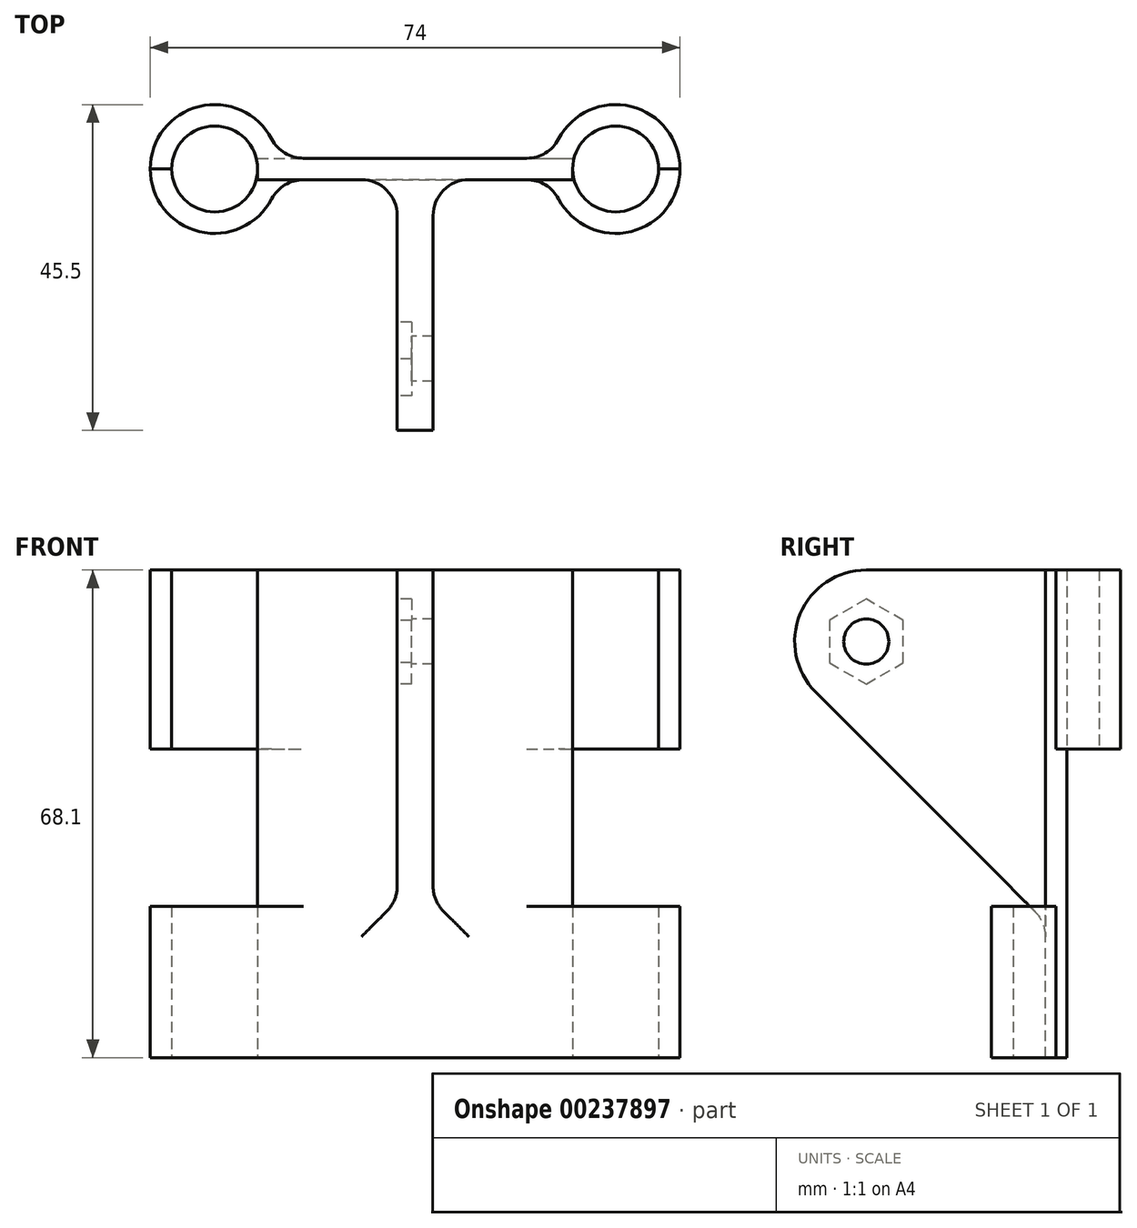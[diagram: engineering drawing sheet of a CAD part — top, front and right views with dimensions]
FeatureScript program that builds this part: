
annotation { "Feature Type Name" : "Feature", "Feature Type Description" : "" }
export const myFeature = defineFeature(function(context is Context, id is Id, definition is map)
    precondition{}
    {
        {
            var Q0;
            Q0=qCreatedBy(makeId("Top.planeOp"),FACE);
            var sketch = newSketch(context, id + "F0", { "sketchPlane" : qUnion([Q0])});
            skArc(sketch, "E0", {"start": v(-34, 0) * mm, "mid": v(-28, -6) * mm, "end": v(-22, 0) * mm});
            skArc(sketch, "E1", {"start": v(22, 0) * mm, "mid": v(28, -6) * mm, "end": v(34, 0) * mm});
            skArc(sketch, "E2", {"start": v(-37, 0) * mm, "mid": v(-28.75, -8.97) * mm, "end": v(-19.13, -1.5) * mm});
            skArc(sketch, "E3", {"start": v(19.13, -1.5) * mm, "mid": v(28.75, -8.97) * mm, "end": v(37, 0) * mm});
            skLineSegment(sketch, "E4", {"start": v(-19.13, -1.5) * mm, "end": v(19.13, -1.5) * mm});
            skLineSegment(sketch, "E5", {"start": v(-37, 0) * mm, "end": v(-34, 0) * mm});
            skLineSegment(sketch, "E6.trimOffspring", {"start": v(34, 0) * mm, "end": v(37, 0) * mm});
            skLineSegment(sketch, "E7", {"start": v(-22, 0) * mm, "end": v(-22, 1.5) * mm});
            skLineSegment(sketch, "E8", {"start": v(-22, 1.5) * mm, "end": v(22, 1.5) * mm});
            skLineSegment(sketch, "E9", {"start": v(22, 1.5) * mm, "end": v(22, 0) * mm});
            skSolve(sketch);
        }
        {
            var Q0;
            Q0=makeQuery(id+"F0.imprint","IMPRINT",FACE,{"disambiguationData":[TD([[makeQuery(id+"F0.imprint","IMPRINT",EDGE,{"derivedFrom":sQuery(id+"F0.wireOp",EDGE,"E0")}),-1.0]])]});
            extrude(context, id + "F1", {"entities" : qUnion([Q0]), "depth" : 21.1 * mm});
        }
        {
            var Q0;
            Q0=makeQuery(id+"F1.opExtrude","CAP_FACE",FACE,{"disambiguationData":[OSD([sQuery(id+"F0.wireOp",EDGE,"E0"),sQuery(id+"F0.wireOp",EDGE,"E1"),sQuery(id+"F0.wireOp",EDGE,"E2"),sQuery(id+"F0.wireOp",EDGE,"E3"),sQuery(id+"F0.wireOp",EDGE,"E4"),sQuery(id+"F0.wireOp",EDGE,"E5"),sQuery(id+"F0.wireOp",EDGE,"95d477b3-e665-48d0-b8e1-d1bc8d960a08.trimOffspring"),sQuery(id+"F0.wireOp",EDGE,"E6.trimOffspring")])],"isStart":false});
            var sketch = newSketch(context, id + "F2", { "sketchPlane" : qUnion([Q0])});
            skLineSegment(sketch, "E10.bottom", {"start": v(-22, -1.5) * mm, "end": v(22, -1.5) * mm});
            skLineSegment(sketch, "E10.top", {"start": v(-22, 1.5) * mm, "end": v(22, 1.5) * mm});
            skLineSegment(sketch, "E10.left", {"start": v(-22, -1.5) * mm, "end": v(-22, 1.5) * mm});
            skLineSegment(sketch, "E10.right", {"start": v(22, -1.5) * mm, "end": v(22, 1.5) * mm});
            skSolve(sketch);
        }
        {
            var Q0;
            Q0=makeQuery(id+"F2.imprint","IMPRINT",FACE,{"disambiguationData":[TD([[makeQuery(id+"F2.imprint","IMPRINT",EDGE,{"derivedFrom":sQuery(id+"F2.wireOp",EDGE,"E10.bottom")}),1.0]])]});
            extrude(context, id + "F3", {"entities" : qUnion([Q0]), "operationType" : NewBodyOperationType.ADD, "depth" : 22 * mm});
        }
        {
            var Q0;
            Q0=makeQuery(id+"F3.opExtrude","CAP_FACE",FACE,{"disambiguationData":[OSD([sQuery(id+"F2.wireOp",EDGE,"E10.bottom"),sQuery(id+"F2.wireOp",EDGE,"E10.top"),sQuery(id+"F2.wireOp",EDGE,"E10.left"),sQuery(id+"F2.wireOp",EDGE,"E10.right")])],"isStart":false});
            var sketch = newSketch(context, id + "F4", { "sketchPlane" : qUnion([Q0])});
            skArc(sketch, "E11", {"start": v(-22, 0) * mm, "mid": v(-28, 6) * mm, "end": v(-34, 0) * mm});
            skArc(sketch, "E12", {"start": v(34, 0) * mm, "mid": v(28, 6) * mm, "end": v(22, 0) * mm});
            skArc(sketch, "E13", {"start": v(-19.13, 1.5) * mm, "mid": v(-28.75, 8.97) * mm, "end": v(-37, 0) * mm});
            skArc(sketch, "E14", {"start": v(37, 0) * mm, "mid": v(28.75, 8.97) * mm, "end": v(19.13, 1.5) * mm});
            skLineSegment(sketch, "E15", {"start": v(-37, 0) * mm, "end": v(-34, 0) * mm});
            skPoint(sketch, "E15.startSnap0", {"position": v(-22, 0) * mm});
            skLineSegment(sketch, "E16", {"start": v(-22, 0) * mm, "end": v(-22, -1.5) * mm});
            skLineSegment(sketch, "E17", {"start": v(-22, -1.5) * mm, "end": v(22, -1.5) * mm});
            skLineSegment(sketch, "E18", {"start": v(22, 0) * mm, "end": v(22, -1.5) * mm});
            skLineSegment(sketch, "E19", {"start": v(34, 0) * mm, "end": v(37, 0) * mm});
            skLineSegment(sketch, "E20", {"start": v(-19.13, 1.5) * mm, "end": v(19.13, 1.5) * mm});
            skSolve(sketch);
        }
        {
            var Q0;
            Q0 = qSketchRegion(id + "F4", true);
            extrude(context, id + "F5", {"entities" : qUnion([Q0]), "operationType" : NewBodyOperationType.ADD, "depth" : 25 * mm});
        }
        {
            var Q0;
            Q0=qCreatedBy(makeId("Right.planeOp"),FACE);
            var sketch = newSketch(context, id + "F6", { "sketchPlane" : qUnion([Q0])});
            skArc(sketch, "E21", {"start": v(-26.5, 68.1) * mm, "mid": v(-35.74, 61.93) * mm, "end": v(-33.57, 51.03) * mm});
            skCircle(sketch, "E22", {"center": v(-26.5, 58.1) * mm, "radius": 3.15 * mm});
            skLineSegment(sketch, "E23", {"start": v(-26.5, 68.1) * mm, "end": v(0, 68.1) * mm});
            skLineSegment(sketch, "E24", {"start": v(0, 68.1) * mm, "end": v(0, 17.46) * mm});
            skLineSegment(sketch, "E25", {"start": v(0, 17.46) * mm, "end": v(-33.57, 51.03) * mm});
            skSolve(sketch);
        }
        {
            var Q0;
            Q0=makeQuery(id+"F6.imprint","IMPRINT",FACE,{"disambiguationData":[TD([[makeQuery(id+"F6.imprint","IMPRINT",EDGE,{"derivedFrom":sQuery(id+"F6.wireOp",EDGE,"E21")}),1.0]])]});
            extrude(context, id + "F7", {"entities" : qUnion([Q0]), "operationType" : NewBodyOperationType.ADD, "depth" : 5 * mm, "symmetric" : true});
        }
        {
            var Q0;
            Q0=makeQuery(id+"F7.opExtrude","CAP_FACE",FACE,{"disambiguationData":[OSD([sQuery(id+"F6.wireOp",EDGE,"E21"),sQuery(id+"F6.wireOp",EDGE,"E22"),sQuery(id+"F6.wireOp",EDGE,"E23"),sQuery(id+"F6.wireOp",EDGE,"E24"),sQuery(id+"F6.wireOp",EDGE,"E25")])],"isStart":true});
            var sketch = newSketch(context, id + "F8", { "sketchPlane" : qUnion([Q0])});
            skCircle(sketch, "E26.cCircle", {"center": v(26.5, 58.1) * mm, "radius": 5.15 * mm, "construction": true});
            skLineSegment(sketch, "E26.0", {"start": v(26.5, 64.05) * mm, "end": v(31.65, 61.07) * mm});
            skLineSegment(sketch, "E26.1", {"start": v(31.65, 61.07) * mm, "end": v(31.65, 55.13) * mm});
            skLineSegment(sketch, "E26.2", {"start": v(31.65, 55.13) * mm, "end": v(26.5, 52.15) * mm});
            skLineSegment(sketch, "E26.3", {"start": v(26.5, 52.15) * mm, "end": v(21.35, 55.13) * mm});
            skLineSegment(sketch, "E26.4", {"start": v(21.35, 55.13) * mm, "end": v(21.35, 61.07) * mm});
            skLineSegment(sketch, "E26.5", {"start": v(21.35, 61.07) * mm, "end": v(26.5, 64.05) * mm});
            skPoint(sketch, "E26.0.midPoint", {"position": v(29.08, 62.56) * mm});
            skSolve(sketch);
        }
        {
            var Q0;
            Q0=makeQuery(id+"F8.imprint","IMPRINT",FACE,{"disambiguationData":[TD([[makeQuery(id+"F8.imprint","IMPRINT",EDGE,{"derivedFrom":sQuery(id+"F8.wireOp",EDGE,"E26.0")}),-1.0]])]});
            extrude(context, id + "F9", {"entities" : qUnion([Q0]), "operationType" : NewBodyOperationType.REMOVE, "oppositeDirection" : true, "depth" : 2 * mm});
        }
        {
            var Q0;
            Q0=makeQuery(id+"F7.boolean.opBoolean","INTERSECT",EDGE,{"derivedFrom":[makeQuery(id+"F5.boolean.opBoolean","MERGE",FACE,{"derivedFrom":[makeQuery(id+"F3.boolean.opBoolean","MERGE",FACE,{"derivedFrom":[makeQuery(id+"F1.opExtrude","SWEPT_FACE",FACE,{"disambiguationData":[OSD([sQuery(id+"F0.wireOp",EDGE,"E4")])]}),makeQuery(id+"F3.opExtrude","SWEPT_FACE",FACE,{"disambiguationData":[OSD([sQuery(id+"F2.wireOp",EDGE,"E10.bottom")])]})]}),makeQuery(id+"F5.opExtrude","SWEPT_FACE",FACE,{"disambiguationData":[OSD([sQuery(id+"F4.wireOp",EDGE,"E17")])]})]}),makeQuery(id+"F7.opExtrude","CAP_FACE",FACE,{"disambiguationData":[OSD([sQuery(id+"F6.wireOp",EDGE,"E21"),sQuery(id+"F6.wireOp",EDGE,"E22"),sQuery(id+"F6.wireOp",EDGE,"E23"),sQuery(id+"F6.wireOp",EDGE,"E24"),sQuery(id+"F6.wireOp",EDGE,"E25")])],"isStart":true})]});
            var Q1;
            Q1=makeQuery(id+"F7.boolean.opBoolean","INTERSECT",EDGE,{"derivedFrom":[makeQuery(id+"F5.boolean.opBoolean","MERGE",FACE,{"derivedFrom":[makeQuery(id+"F3.boolean.opBoolean","MERGE",FACE,{"derivedFrom":[makeQuery(id+"F1.opExtrude","SWEPT_FACE",FACE,{"disambiguationData":[OSD([sQuery(id+"F0.wireOp",EDGE,"E4")])]}),makeQuery(id+"F3.opExtrude","SWEPT_FACE",FACE,{"disambiguationData":[OSD([sQuery(id+"F2.wireOp",EDGE,"E10.bottom")])]})]}),makeQuery(id+"F5.opExtrude","SWEPT_FACE",FACE,{"disambiguationData":[OSD([sQuery(id+"F4.wireOp",EDGE,"E17")])]})]}),makeQuery(id+"F7.opExtrude","CAP_FACE",FACE,{"disambiguationData":[OSD([sQuery(id+"F6.wireOp",EDGE,"E21"),sQuery(id+"F6.wireOp",EDGE,"E22"),sQuery(id+"F6.wireOp",EDGE,"E23"),sQuery(id+"F6.wireOp",EDGE,"E24"),sQuery(id+"F6.wireOp",EDGE,"E25")])],"isStart":false})]});
            fillet(context, id + "F10", {"entities" : qUnion([Q0, Q1]), "radius" : 5 * mm, "tangentPropagation" : true, "allowEdgeOverflow" : false});
        }
        {
            var Q0;
            Q0=makeQuery(id+"F7.boolean.opBoolean","INTERSECT",EDGE,{"derivedFrom":[makeQuery(id+"F5.boolean.opBoolean","MERGE",FACE,{"derivedFrom":[makeQuery(id+"F3.boolean.opBoolean","MERGE",FACE,{"derivedFrom":[makeQuery(id+"F1.opExtrude","SWEPT_FACE",FACE,{"disambiguationData":[OSD([sQuery(id+"F0.wireOp",EDGE,"E4")])]}),makeQuery(id+"F3.opExtrude","SWEPT_FACE",FACE,{"disambiguationData":[OSD([sQuery(id+"F2.wireOp",EDGE,"E10.bottom")])]})]}),makeQuery(id+"F5.opExtrude","SWEPT_FACE",FACE,{"disambiguationData":[OSD([sQuery(id+"F4.wireOp",EDGE,"E17")])]})]}),makeQuery(id+"F7.opExtrude","SWEPT_FACE",FACE,{"disambiguationData":[OSD([sQuery(id+"F6.wireOp",EDGE,"E25")])]})]});
            fillet(context, id + "F11", {"entities" : qUnion([Q0]), "radius" : 5 * mm, "tangentPropagation" : true, "allowEdgeOverflow" : false});
        }
        {
            var Q0;
            Q0=makeQuery(id+"F1.opExtrude","SWEPT_EDGE",EDGE,{"disambiguationData":[OSD([sQuery(id+"F0.wireOp",EDGE,"E2"),sQuery(id+"F0.wireOp",EDGE,"E4")])]});
            var Q1;
            Q1=makeQuery(id+"F1.opExtrude","SWEPT_EDGE",EDGE,{"disambiguationData":[OSD([sQuery(id+"F0.wireOp",EDGE,"E3"),sQuery(id+"F0.wireOp",EDGE,"E4")])]});
            var Q2;
            Q2=makeQuery(id+"F5.opExtrude","SWEPT_EDGE",EDGE,{"disambiguationData":[OSD([sQuery(id+"F2.wireOp",EDGE,"E10.top"),sQuery(id+"F4.wireOp",EDGE,"E13"),sQuery(id+"F4.wireOp",EDGE,"E20")])]});
            var Q3;
            Q3=makeQuery(id+"F5.opExtrude","SWEPT_EDGE",EDGE,{"disambiguationData":[OSD([sQuery(id+"F2.wireOp",EDGE,"E10.top"),sQuery(id+"F4.wireOp",EDGE,"E14"),sQuery(id+"F4.wireOp",EDGE,"E20")])]});
            fillet(context, id + "F12", {"entities" : qUnion([Q0, Q1, Q2, Q3]), "radius" : 5 * mm, "tangentPropagation" : true, "allowEdgeOverflow" : false});
        }
    });
